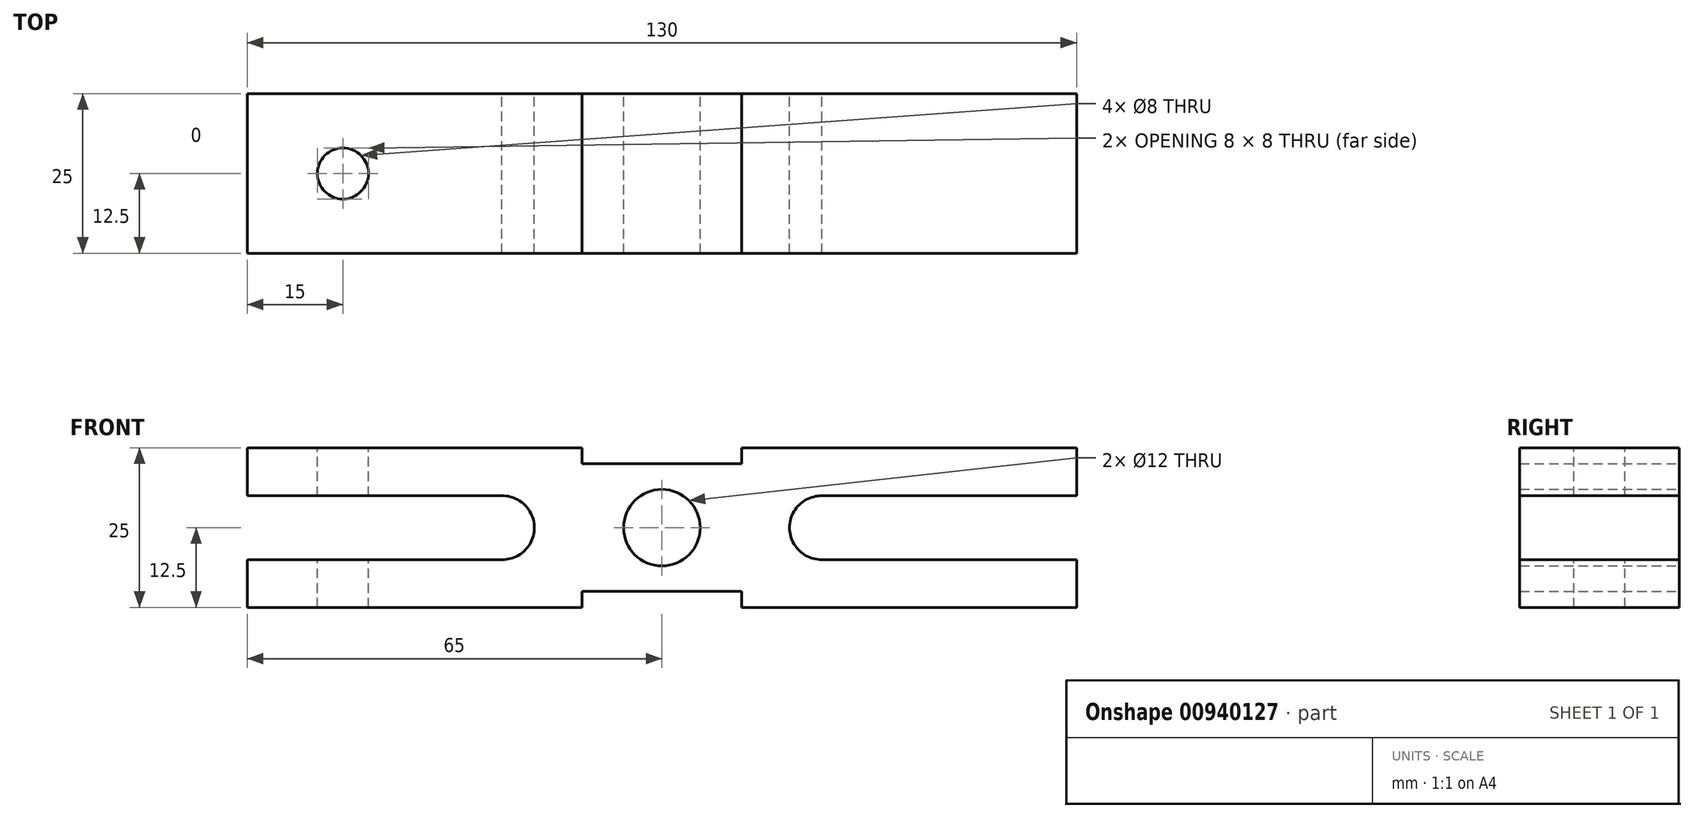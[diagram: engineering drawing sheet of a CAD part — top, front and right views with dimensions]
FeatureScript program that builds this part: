
annotation { "Feature Type Name" : "Feature", "Feature Type Description" : "" }
export const myFeature = defineFeature(function(context is Context, id is Id, definition is map)
    precondition{}
    {
        {
            var Q0;
            Q0=qCreatedBy(makeId("Front.planeOp"),FACE);
            var sketch = newSketch(context, id + "F0", { "sketchPlane" : qUnion([Q0])});
            skLineSegment(sketch, "E0.bottom", {"start": v(-65, 12.5) * mm, "end": v(-12.5, 12.5) * mm});
            skLineSegment(sketch, "E0.top", {"start": v(-65, -12.5) * mm, "end": v(-12.5, -12.5) * mm});
            skLineSegment(sketch, "E0.left", {"start": v(-65, 12.5) * mm, "end": v(-65, 5) * mm});
            skLineSegment(sketch, "E0.right", {"start": v(65, 12.5) * mm, "end": v(65, 5) * mm});
            skPoint(sketch, "E0.middle", {"position": v(0, 0) * mm});
            skLineSegment(sketch, "E1", {"start": v(0, 0) * mm, "end": v(0, 10) * mm});
            skLineSegment(sketch, "E2", {"start": v(12.5, 12.5) * mm, "end": v(12.5, 10) * mm});
            skLineSegment(sketch, "E3", {"start": v(12.5, 10) * mm, "end": v(-12.5, 10) * mm});
            skLineSegment(sketch, "E4", {"start": v(-12.5, 10) * mm, "end": v(-12.5, 12.5) * mm});
            skLineSegment(sketch, "E5.MirrorCS", {"start": v(12.5, -10) * mm, "end": v(-12.5, -10) * mm});
            skLineSegment(sketch, "E6.MirrorCS", {"start": v(12.5, -12.5) * mm, "end": v(12.5, -10) * mm});
            skLineSegment(sketch, "E7.MirrorCS", {"start": v(-12.5, -10) * mm, "end": v(-12.5, -12.5) * mm});
            skLineSegment(sketch, "E8.trimOffspring", {"start": v(12.5, 12.5) * mm, "end": v(65, 12.5) * mm});
            skPoint(sketch, "E9.start.orphan", {"position": v(0, 12.5) * mm});
            skLineSegment(sketch, "E10.trimOffspring", {"start": v(12.5, -12.5) * mm, "end": v(65, -12.5) * mm});
            skCircle(sketch, "E11", {"center": v(0, 0) * mm, "radius": 6 * mm});
            skArc(sketch, "E12", {"start": v(-25.08, -5) * mm, "mid": v(-20, 0) * mm, "end": v(-25.1, 5) * mm});
            skLineSegment(sketch, "E13", {"start": v(-25.1, 5) * mm, "end": v(-65, 5) * mm});
            skLineSegment(sketch, "E14", {"start": v(-25.08, -5) * mm, "end": v(-65, -5) * mm});
            skPoint(sketch, "E15.start.orphan", {"position": v(-65, 0) * mm});
            skLineSegment(sketch, "E16.trimOffspring", {"start": v(-65, -5) * mm, "end": v(-65, -12.5) * mm});
            skLineSegment(sketch, "E17.MirrorCS", {"start": v(25.1, 5) * mm, "end": v(65, 5) * mm});
            skArc(sketch, "E18.MirrorCS", {"start": v(25.08, -5) * mm, "mid": v(20, 0) * mm, "end": v(25.1, 5) * mm});
            skLineSegment(sketch, "E19.MirrorCS", {"start": v(25.08, -5) * mm, "end": v(65, -5) * mm});
            skLineSegment(sketch, "E20.trimOffspring", {"start": v(65, -5) * mm, "end": v(65, -12.5) * mm});
            skSolve(sketch);
        }
        {
            var Q0;
            Q0=makeQuery(id+"F0.imprint","IMPRINT",FACE,{"disambiguationData":[TD([[makeQuery(id+"F0.imprint","IMPRINT",EDGE,{"derivedFrom":sQuery(id+"F0.wireOp",EDGE,"E0.bottom")}),-1.0]])]});
            extrude(context, id + "F1", {"entities" : qUnion([Q0]), "depth" : 25 * mm, "offsetDistance" : 25 * mm});
        }
        {
            var Q0;
            Q0=qCreatedBy(makeId("Top.planeOp"),FACE);
            var sketch = newSketch(context, id + "F2", { "sketchPlane" : qUnion([Q0])});
            skCircle(sketch, "E21", {"center": v(-50, -12.5) * mm, "radius": 4 * mm});
            skCircle(sketch, "E22.MirrorC", {"center": v(50, -12.5) * mm, "radius": 4 * mm});
            skSolve(sketch);
        }
        {
            var Q0;
            Q0=makeQuery(id+"F2.imprint","IMPRINT",FACE,{"disambiguationData":[TD([[makeQuery(id+"F2.imprint","IMPRINT",EDGE,{"derivedFrom":sQuery(id+"F2.wireOp",EDGE,"E21")}),1.0]])]});
            var Q1;
            Q1=makeQuery(id+"F2.imprint","IMPRINT",FACE,{"disambiguationData":[TD([[makeQuery(id+"F2.imprint","IMPRINT",EDGE,{"derivedFrom":sQuery(id+"F2.wireOp",EDGE,"E22.MirrorC")}),-1.0]])]});
            extrude(context, id + "F3", {"entities" : qUnion([Q0, Q1]), "operationType" : NewBodyOperationType.REMOVE, "endBound" : BoundingType.SYMMETRIC, "oppositeDirection" : true, "depth" : 25 * mm, "offsetDistance" : 25 * mm});
        }
    });
